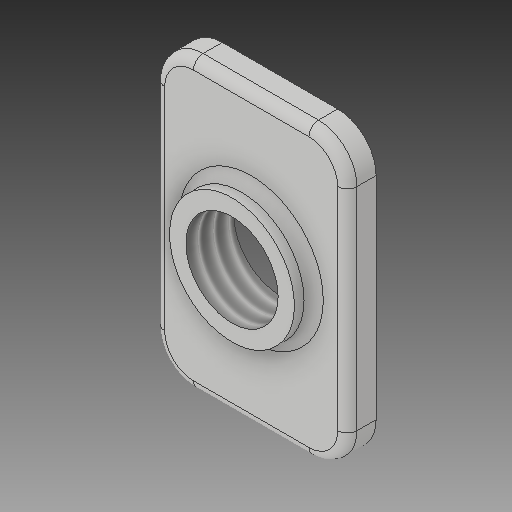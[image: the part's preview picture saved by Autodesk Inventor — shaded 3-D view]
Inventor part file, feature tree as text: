
AUTODESK INVENTOR PART (.ipt)
format: ipt  version: 2017 (Build 210142000, 142)  size: 163,328 bytes
history: native  units: mm
features: other x3, sketch x2
ambient origin geometry x8: Origin, YZ Plane, XZ Plane, XY Plane, X Axis, Y Axis, Z Axis, Center Point
bodies: Solid1 (feature_tree)
feature tree (5):
  other  "M5 Tee Nut_MIR_MIR_MIR_MIR_MIR.ipt"
  other  "Solid1::M5 Tee Nut_MIR_MIR_MIR_MIR_MIR.ipt"
  other  "TaggingFeature1"
  sketch  "Sketch1"  dims[d0=10.0mm]
  sketch  "Sketch2"
